# Revit family: Pantalla Modelo GS_LPVM16.1
name_source: partatom
category: Luminarias
units: mm (PartAtom-declared; Revit-internal decimal feet)

## family parameters
Compartido = No
Corte con vacíos al cargar = No
Cota de conector redondo = Diámetro de uso
Origen de luz = No
Punto de cálculo de habitación = No
Se basa en plano de trabajo = Sí
Siempre vertical = No
Tipo de pieza = Normal

## types (1)
- Pantalla Modelo GS_LPVM16.1
    Comentarios de vataje = 110-240V
    Descripción = PANTALLA CON UN LED TAIWAN EPISTAR CHIP, QUE PERMITE EL VIENTO Y LA LUZ DEL SOL PASEN A TRAVES DE LA PANTALLA AL INTERIOR DEL EDIFICIO. INSTALACION DIABLE, SENCILLA Y RAPIDA, UNA SOLA TIRA REEMPLAZABLE, DE FACIL MANTENIMIENTO Y AHORRO DE ENERGIA DEL 60%. PIXEL PITCH 16MM, DIMENSIONES DEL PANEL 1200X1200MM, RESOLUCION DE 72X36 DOT, CONFIGURACION DEL PIXEL EN 2R1G1B, CANTIDAD POR PANEL DE LED 2592 DOT, PESO 36kg/PANEL, CONSUMO DE ENERGIA DE 600W/PANEL, TEMPERATURA DE COLOR EN 5000K, DISTANCIA DE VISUALIZACION 16M, BRILLO DE 5000-6000 NIT, TRANSPARENCIA DEL 30%, ESTRUCTURA DEL PANEL EN ALEACION DE ALUMINIO, VELOCIDAD DE ACTUALIZACION EN 1600Hz, VOLTAJE EN AC 110-240V/5060Hz, ANGULO DE VISUALIZACION 120/60 GRADOS, SISTEMA DE CONTROL ONLINE O PC, MODO DRIVE CORRIENTE COSNTANTE, HORAS DE VIDA <50000 HORAS, IP 65, TEMPERATURA DE OPERACIÓN -10C + 40C Y COMO MAXIMO -20C +50C, HUMEDAD 10-90%, SISTEMA OPERATIVO WINDOWS 2000/XP/VISTA/WINDOWS 7, TIPO DE SEÑAL AV/S-VIDEO/VGA/CVBS/HDMI/DVI, CONTROL DE DISTANCIA HSYV, 100M. REQUIERE ACCESORIOS COMO CONTROLADOR DE SISTEMA (XLV16V.1).
    Elevación por defecto = 0 mm  [stored 0 ft]
    Espesor = 1 mm  [stored 0.00328084 ft]
    Fabricante = BRILLANT
    Lámpara = Taiwan Epistar Chip
    Modelo = LPVM16.1
    Modulo alto = 1200 mm  [stored 3.93701 ft]
    Modulo largo = 1200 mm  [stored 3.93701 ft]
    Watt per fixture = 600

note: [stored X ft] marks values corroborated as IEEE doubles in the binary element streams (Revit-internal decimal feet)

## geometry (parser evidence)
native form markers: Blend x2
no freeform markers — native parametric forms only
